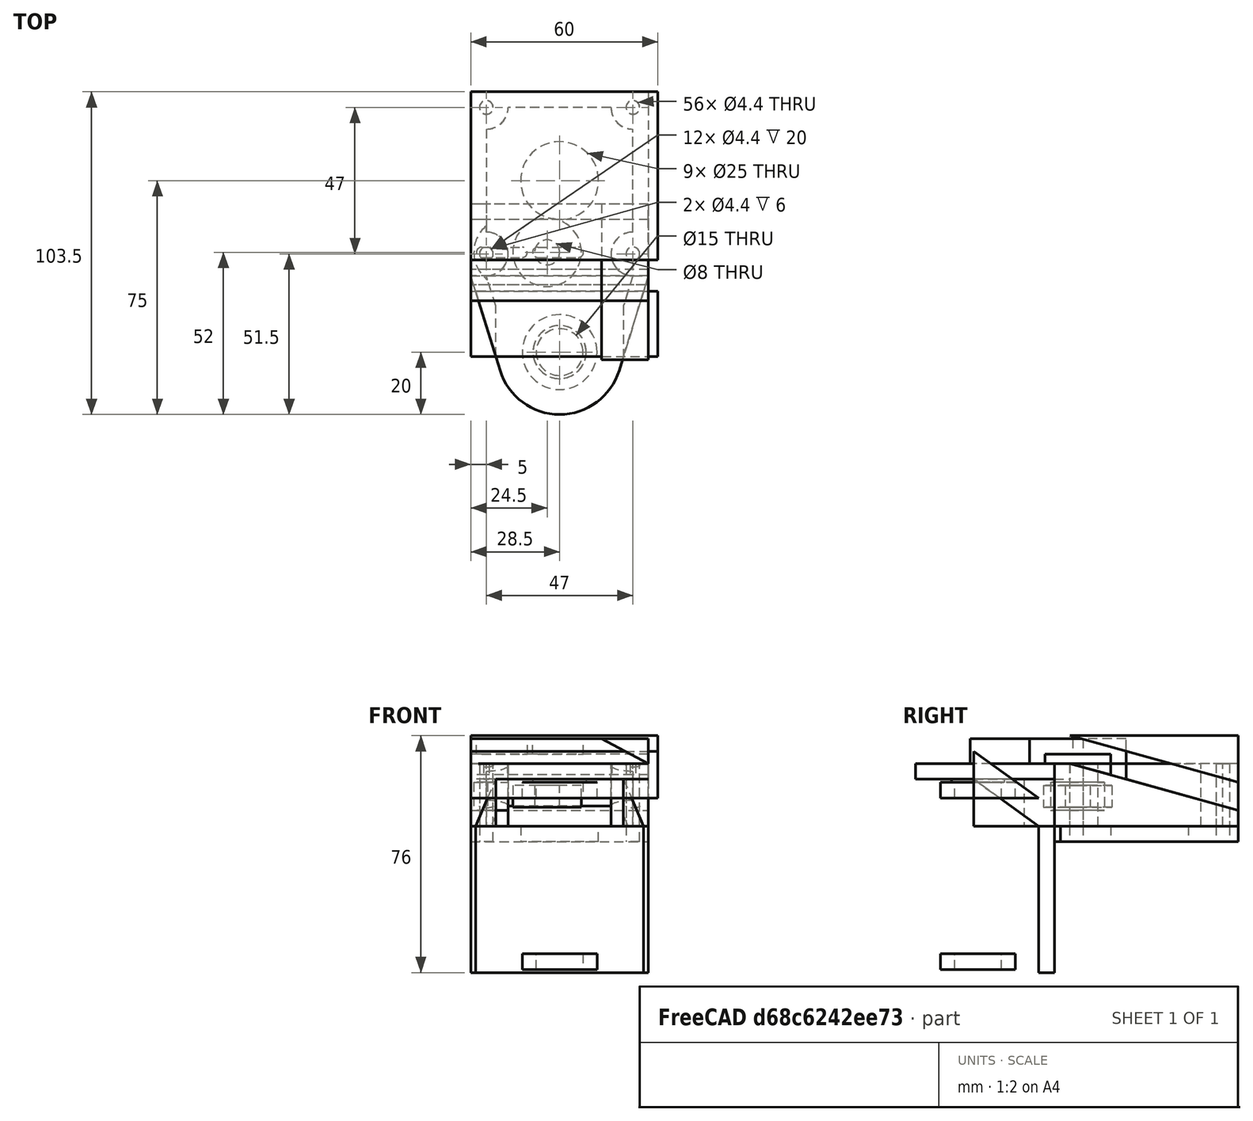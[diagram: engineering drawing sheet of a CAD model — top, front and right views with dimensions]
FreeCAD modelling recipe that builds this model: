
FCSTD DOCUMENT  (FreeCAD 0.16R6700 (Git))
Label: string_drive2_full
License: All rights reserved
LicenseURL: http://en.wikipedia.org/wiki/All_rights_reserved
objects: Sketcher::SketchObject×17, PartDesign::Pad×12, PartDesign::Pocket×5, Mesh::Feature×3, Part::Cylinder×1, Part::FeaturePython×1, Part::Cut×1
note: 54 computed .brp shape members not serialized (recipe doc carries the construction recipe); baked Part::Feature solids carry a one-line shape summary decoded from their .brp

FEATURE [Mesh::Feature] string_guide_full
FEATURE [Part::Cylinder] Cylinder
  Angle = 360
  Height = 5
  Placement = pos=(0,0,5) rot=(0,0,1;0rad)
  Radius = 12
FEATURE [Sketcher::SketchObject] Sketch
  Placement = pos=(0,0,10) rot=(0,0,1;0rad)
  Support = -> Cylinder [Face2]
  sketch-geometry (1):
    g0: Circle CenterX=0 CenterY=0 CenterZ=0 NormalX=0 NormalY=0 NormalZ=1 Radius=7.5
  constraints (2):
    c: Coincident(g0,g-1)
    c: Radius(g0) = 7.5
FEATURE [PartDesign::Pocket] Pocket  label="bearing 6802"
  Length = 5
  Placement = pos=(0,0,5) rot=(0,0,1;0rad)
  Sketch = -> Sketch
  Type = 0
FEATURE [Part::FeaturePython] Clone  label="Clone of bearing 6802"  # Draft clone (typed FeaturePython)
  Objects = -> [Pocket]
  Placement = pos=(0,0,-50) rot=(0,0,1;0rad)
  Scale = (1,1,1)
FEATURE [Mesh::Feature] nema23_76  label="nema23-76"
  Placement = pos=(0,55,-8) rot=(1,0,0;3.14159rad)
FEATURE [Sketcher::SketchObject] Sketch001
  Placement = pos=(0,0,-9) rot=(0,0,1;0rad)
  sketch-geometry (13):
    g0: Circle CenterX=23.5 CenterY=31.5 CenterZ=0 NormalX=0 NormalY=0 NormalZ=1 Radius=2.2
    g1: Circle CenterX=23.5 CenterY=78.5 CenterZ=0 NormalX=0 NormalY=0 NormalZ=1 Radius=2.2
    g2: Circle CenterX=-23.5 CenterY=78.5 CenterZ=0 NormalX=0 NormalY=0 NormalZ=1 Radius=2.2
    g3: Circle CenterX=-23.5 CenterY=31.5 CenterZ=0 NormalX=0 NormalY=0 NormalZ=1 Radius=2.2
    g4: LineSegment [constr] StartX=-23.5 StartY=78.5 StartZ=0 EndX=23.5 EndY=78.5 EndZ=0
    g5: LineSegment [constr] StartX=-23.5 StartY=78.5 StartZ=0 EndX=-23.5 EndY=31.5 EndZ=0
    g6: LineSegment [constr] StartX=-23.5 StartY=31.5 StartZ=0 EndX=23.5 EndY=31.5 EndZ=0
    g7: LineSegment [constr] StartX=23.5 StartY=78.5 StartZ=0 EndX=23.5 EndY=31.5 EndZ=0
    g8: Circle CenterX=0 CenterY=55 CenterZ=0 NormalX=0 NormalY=0 NormalZ=1 Radius=12.5
    g9: LineSegment StartX=-28.5 StartY=83.5 StartZ=0 EndX=28.5 EndY=83.5 EndZ=0
    g10: LineSegment StartX=28.5 StartY=83.5 StartZ=0 EndX=28.5 EndY=26.5 EndZ=0
    g11: LineSegment StartX=28.5 StartY=26.5 StartZ=0 EndX=-28.5 EndY=26.5 EndZ=0
    g12: LineSegment StartX=-28.5 StartY=26.5 StartZ=0 EndX=-28.5 EndY=83.5 EndZ=0
  constraints (35):
    c: Radius(g1) = 2.2
    c: Equal(g1,g2)
    c: Equal(g2,g3)
    c: Equal(g0,g3)
    c: Coincident(g1,g4)
    c: Coincident(g2,g4)
    c: Horizontal(g4)
    c: Coincident(g3,g5)
    c: Coincident(g2,g5)
    c: Vertical(g5)
    c: Coincident(g0,g6)
    c: Coincident(g3,g6)
    c: Horizontal(g6)
    c: Coincident(g0,g7)
    c: Coincident(g1,g7)
    c: Vertical(g7)
    c: DistanceY(g-1,g0) = 31.5
    c: DistanceX(g-1,g0) = 23.5
    c: DistanceX(g3,g0) = 47
    c: DistanceY(g3,g2) = 47
    c: PointOnObject(g8,g-2)
    c: DistanceY(g3,g8) = 23.5
    c: Radius(g8) = 12.5
    c: Coincident(g9,g10)
    c: Coincident(g10,g11)
    c: Coincident(g11,g12)
    c: Coincident(g12,g9)
    c: Horizontal(g9)
    c: Horizontal(g11)
    c: Vertical(g10)
    c: Vertical(g12)
    c: DistanceX(g0,g10) = 5
    c: DistanceY(g10,g0) = 5
    c: DistanceX(g9,g2) = 5
    c: DistanceY(g2,g9) = 5
FEATURE [PartDesign::Pad] Pad
  Length = 5
  Length2 = 100
  Placement = pos=(0,0,-9) rot=(0,0,1;0rad)
  Sketch = -> Sketch001
  Type = 0
FEATURE [Sketcher::SketchObject] Sketch002
  ExternalGeometry = -> [Pad]
  Placement = pos=(0,0,-4) rot=(0,0,1;0rad)
  Support = -> Pad [Face11]
  sketch-geometry (18):
    g0: LineSegment StartX=-28.5 StartY=24.5 StartZ=0 EndX=-28.5 EndY=83.5 EndZ=0
    g1: LineSegment StartX=-28.5 StartY=83.5 StartZ=0 EndX=28.5 EndY=83.5 EndZ=0
    g2: LineSegment StartX=28.5 StartY=83.5 StartZ=0 EndX=28.5 EndY=24.5 EndZ=0
    g3: LineSegment StartX=28.5 StartY=24.5 StartZ=0 EndX=23.5 EndY=24.5 EndZ=0
    g4: LineSegment StartX=23.5 StartY=38.5 StartZ=0 EndX=23.5 EndY=71.5 EndZ=0
    g5: LineSegment StartX=16.5 StartY=78.5 StartZ=0 EndX=-16.5 EndY=78.5 EndZ=0
    g6: LineSegment StartX=-23.5 StartY=71.5 StartZ=0 EndX=-23.5 EndY=38.5 EndZ=0
    g7: LineSegment StartX=-23.5 StartY=24.5 StartZ=0 EndX=-28.5 EndY=24.5 EndZ=0
    g8: ArcOfCircle CenterX=23.5 CenterY=78.5 CenterZ=0 NormalX=0 NormalY=0 NormalZ=1 Radius=7 StartAngle=3.14159 EndAngle=4.71239
    g9: ArcOfCircle CenterX=-23.5 CenterY=78.5 CenterZ=0 NormalX=0 NormalY=0 NormalZ=1 Radius=7 StartAngle=4.71239 EndAngle=6.28319
    g10: ArcOfCircle CenterX=-23.5 CenterY=31.5 CenterZ=0 NormalX=0 NormalY=0 NormalZ=1 Radius=7 StartAngle=4.71239 EndAngle=7.85398
    g11: ArcOfCircle CenterX=23.5 CenterY=31.5 CenterZ=0 NormalX=0 NormalY=0 NormalZ=1 Radius=7 StartAngle=1.5708 EndAngle=4.71239
    g12: LineSegment [constr] StartX=23.5 StartY=38.5 StartZ=0 EndX=23.5 EndY=24.5 EndZ=0
    g13: LineSegment [constr] StartX=-23.5 StartY=38.5 StartZ=0 EndX=-23.5 EndY=24.5 EndZ=0
    g14: Circle CenterX=-23.5 CenterY=78.5 CenterZ=0 NormalX=0 NormalY=0 NormalZ=1 Radius=2.2
    g15: Circle CenterX=23.5 CenterY=78.5 CenterZ=0 NormalX=0 NormalY=0 NormalZ=1 Radius=2.2
    g16: Circle CenterX=23.5 CenterY=31.5 CenterZ=0 NormalX=0 NormalY=0 NormalZ=1 Radius=2.2
    g17: Circle CenterX=-23.5 CenterY=31.5 CenterZ=0 NormalX=0 NormalY=0 NormalZ=1 Radius=2.2
  constraints (46):
    c: Coincident(g0,g1)
    c: Coincident(g1,g2)
    c: Coincident(g-4,g0)
    c: Coincident(g-5,g1)
    c: Horizontal(g7)
    c: Horizontal(g3)
    c: Vertical(g4)
    c: Vertical(g6)
    c: Horizontal(g5)
    c: Radius(g8) = 7
    c: Coincident(g8,g-7)
    c: DistanceX(g3,g3) = 5
    c: DistanceX(g7,g7) = 5
    c: Coincident(g5,g8)
    c: Coincident(g4,g8)
    c: Coincident(g6,g9)
    c: Coincident(g5,g9)
    c: DistanceY(g5,g0) = 5
    c: Radius(g9) = 7
    c: Coincident(g9,g-6)
    c: Coincident(g10,g-8)
    c: Radius(g10) = 7
    c: Equal(g10,g11) = 7
    c: Coincident(g11,g-9)
    c: Coincident(g4,g11)
    c: Coincident(g6,g10)
    c: Coincident(g3,g12)
    c: Coincident(g4,g12)
    c: Vertical(g12)
    c: Coincident(g7,g13)
    c: Coincident(g6,g13)
    c: Vertical(g13)
    c: Coincident(g14,g9)
    c: Radius(g14) = 2.2
    c: Coincident(g8,g15)
    c: Radius(g15) = 2.2
    c: Coincident(g11,g16)
    c: Radius(g16) = 2.2
    c: Coincident(g10,g17)
    c: Radius(g17) = 2.2
    c: Coincident(g0,g7)
    c: Coincident(g7,g10)
    c: Vertical(g0)
    c: Coincident(g2,g3)
    c: Coincident(g11,g3)
    c: Vertical(g2)
FEATURE [PartDesign::Pad] Pad001
  Length = 20
  Length2 = 100
  Placement = pos=(0,0,-9) rot=(0,0,1;0rad)
  Sketch = -> Sketch002
  Type = 0
FEATURE [Sketcher::SketchObject] Sketch005
  ExternalGeometry = -> [Pad001]
  Placement = pos=(-28.5,0,-9) rot=(0.57735,-0.57735,-0.57735;2.0944rad)
  Support = -> Pad001 [Face16]
  sketch-geometry (5):
    g0: LineSegment StartX=-83.5 StartY=25 StartZ=0 EndX=-29.5 EndY=25 EndZ=0
    g1: LineSegment StartX=-29.5 StartY=25 StartZ=0 EndX=-83.5 EndY=10 EndZ=0
    g2: LineSegment StartX=-83.5 StartY=10 StartZ=0 EndX=-83.5 EndY=25 EndZ=0
    g3: LineSegment [constr] StartX=-83.5 StartY=5 StartZ=0 EndX=-83.5 EndY=10 EndZ=0
    g4: LineSegment [constr] StartX=-29.5 StartY=25 StartZ=0 EndX=-24.5 EndY=25 EndZ=0
  constraints (12):
    c: Coincident(g0,g2)
    c: Coincident(g0,g-4)
    c: Coincident(g1,g2)
    c: Coincident(g1,g3)
    c: Vertical(g3)
    c: Coincident(g3,g-4)
    c: DistanceY(g3,g3) = 5
    c: Coincident(g0,g1)
    c: Coincident(g4,g-3)
    c: Coincident(g4,g0)
    c: Distance(g4) = 5
    c: Horizontal(g4)
FEATURE [PartDesign::Pocket] Pocket001
  Length = 60
  Placement = pos=(0,0,-9) rot=(0,0,1;0rad)
  Sketch = -> Sketch005
  Type = 0
FEATURE [Sketcher::SketchObject] Sketch006
  ExternalGeometry = -> [Pocket001]
  Placement = pos=(0,0,16) rot=(0,0,1;0rad)
  Support = -> Pocket001 [Face32]
  sketch-geometry (6):
    g0: LineSegment StartX=-28.5 StartY=29.5 StartZ=0 EndX=28.5 EndY=29.5 EndZ=0
    g1: LineSegment StartX=28.5 StartY=29.5 StartZ=0 EndX=28.5 EndY=24.5 EndZ=0
    g2: LineSegment StartX=28.5 StartY=24.5 StartZ=0 EndX=19.1092 EndY=-5.90251 EndZ=0
    g3: LineSegment StartX=-19.1092 StartY=-5.90251 StartZ=0 EndX=-28.5 EndY=24.5 EndZ=0
    g4: LineSegment StartX=-28.5 StartY=24.5 StartZ=0 EndX=-28.5 EndY=29.5 EndZ=0
    g5: ArcOfCircle CenterX=0 CenterY=0 CenterZ=0 NormalX=0 NormalY=0 NormalZ=1 Radius=20 StartAngle=3.44118 EndAngle=5.9836
  constraints (12):
    c: Coincident(g1,g2)
    c: Coincident(g3,g4)
    c: Coincident(g0,g4)
    c: Coincident(g0,g1)
    c: Coincident(g0,g-4)
    c: Coincident(g1,g-4)
    c: Coincident(g0,g-3)
    c: Coincident(g3,g-3)
    c: Tangent(g3,g5) = 1.5708
    c: Tangent(g2,g5) = 1.5708
    c: Coincident(g5,g-1)
    c: Radius(g5) = 20
FEATURE [PartDesign::Pad] Pad002
  Length = 5
  Length2 = 100
  Placement = pos=(0,0,-9) rot=(0,0,1;0rad)
  Reversed = true
  Sketch = -> Sketch006
  Type = 0
FEATURE [Sketcher::SketchObject] Sketch007
  ExternalGeometry = -> [Pad002]
  Placement = pos=(0,0,11) rot=(1,0,0;3.14159rad)
  Support = -> Pad002 [Face39]
  sketch-geometry (8):
    g0: LineSegment StartX=-28.5 StartY=-24.5 StartZ=0 EndX=-20.5 EndY=1.39974 EndZ=0
    g1: LineSegment StartX=-20.5 StartY=1.39974 StartZ=0 EndX=-20.5 EndY=-14.7876 EndZ=0
    g2: LineSegment StartX=-20.5 StartY=-14.7876 StartZ=0 EndX=-23.5 EndY=-24.5 EndZ=0
    g3: LineSegment StartX=-23.5 StartY=-24.5 StartZ=0 EndX=-28.5 EndY=-24.5 EndZ=0
    g4: LineSegment StartX=28.5 StartY=-24.5 StartZ=0 EndX=23.5 EndY=-24.5 EndZ=0
    g5: LineSegment StartX=23.5 StartY=-24.5 StartZ=0 EndX=20.5 EndY=-14.7876 EndZ=0
    g6: LineSegment StartX=20.5 StartY=-14.7876 StartZ=0 EndX=20.5 EndY=1.39974 EndZ=0
    g7: LineSegment StartX=20.5 StartY=1.39974 StartZ=0 EndX=28.5 EndY=-24.5 EndZ=0
  constraints (22):
    c: Coincident(g0,g1)
    c: Coincident(g1,g2)
    c: Coincident(g2,g3)
    c: Coincident(g3,g0)
    c: Horizontal(g3)
    c: DistanceX(g3,g3) = 5
    c: Coincident(g0,g-5)
    c: PointOnObject(g0,g-5)
    c: Parallel(g-5,g2)
    c: Vertical(g1)
    c: DistanceX(g2,g1) = 3
    c: Coincident(g4,g5)
    c: Coincident(g5,g6)
    c: Coincident(g6,g7)
    c: Coincident(g7,g4)
    c: Horizontal(g4)
    c: DistanceX(g4,g4) = 5
    c: DistanceX(g5,g4) = 3
    c: Vertical(g6)
    c: Coincident(g4,g-6)
    c: PointOnObject(g6,g-6)
    c: Parallel(g-6,g5)
FEATURE [PartDesign::Pad] Pad003
  Length = 15
  Length2 = 100
  Placement = pos=(0,0,-9) rot=(0,0,1;0rad)
  Sketch = -> Sketch007
  Type = 0
FEATURE [Sketcher::SketchObject] Sketch008
  ExternalGeometry = -> [Pad003]
  Placement = pos=(-28.5,0,-9) rot=(0.57735,-0.57735,-0.57735;2.0944rad)
  Support = -> Pad003 [Face16]
  sketch-geometry (4):
    g0: LineSegment StartX=-19.5 StartY=5 StartZ=0 EndX=1.39974 EndY=20 EndZ=0
    g1: LineSegment StartX=1.39974 StartY=20 StartZ=0 EndX=1.39974 EndY=5 EndZ=0
    g2: LineSegment StartX=1.39974 StartY=5 StartZ=0 EndX=-19.5 EndY=5 EndZ=0
    g3: LineSegment [constr] StartX=-24.5 StartY=5 StartZ=0 EndX=-19.5 EndY=5 EndZ=0
  constraints (9):
    c: Coincident(g0,g1)
    c: Coincident(g1,g2)
    c: Coincident(g0,g-4)
    c: Coincident(g1,g-4)
    c: Coincident(g0,g2)
    c: Coincident(g0,g3)
    c: Horizontal(g3)
    c: DistanceX(g3,g3) = 5
    c: Coincident(g3,g-3)
FEATURE [PartDesign::Pocket] Pocket002
  Length = 60
  Placement = pos=(0,0,-9) rot=(0,0,1;0rad)
  Sketch = -> Sketch008
  Type = 0
FEATURE [Sketcher::SketchObject] Sketch009
  Placement = pos=(0,0,11) rot=(1,0,0;3.14159rad)
  Support = -> Pocket002 [Face45]
  sketch-geometry (1):
    g0: Circle CenterX=0 CenterY=0 CenterZ=0 NormalX=0 NormalY=0 NormalZ=1 Radius=8.5
  constraints (2):
    c: Coincident(g0,g-1)
    c: Radius(g0) = 8.5
FEATURE [PartDesign::Pad] Pad004
  Length = 1
  Length2 = 100
  Placement = pos=(0,0,-9) rot=(0,0,1;0rad)
  Sketch = -> Sketch009
  Type = 0
FEATURE [Sketcher::SketchObject] Sketch010
  Placement = pos=(-20.5,0,-9) rot=(0.57735,0.57735,0.57735;2.0944rad)
  Support = -> Pad004 [Face55]
  sketch-geometry (1):
    g0: Circle CenterX=0 CenterY=0 CenterZ=0 NormalX=0 NormalY=0 NormalZ=1 Radius=7.5
  constraints (2):
    c: Coincident(g0,g-1)
    c: Radius(g0) = 7.5
FEATURE [PartDesign::Pad] Pad005
  Length = 5
  Length2 = 100
  Placement = pos=(0,0,-9) rot=(0,0,1;0rad)
  Sketch = -> Sketch010
  Type = 0
FEATURE [Sketcher::SketchObject] Sketch011
  ExternalGeometry = -> [Pad005]
  Placement = pos=(0,0,-4) rot=(1,0,0;3.14159rad)
  Support = -> Pad005 [Face13]
  sketch-geometry (4):
    g0: LineSegment StartX=-28.5 StartY=-24.5 StartZ=0 EndX=28.5 EndY=-24.5 EndZ=0
    g1: LineSegment StartX=28.5 StartY=-24.5 StartZ=0 EndX=26.9556 EndY=-19.5 EndZ=0
    g2: LineSegment StartX=26.9556 StartY=-19.5 StartZ=0 EndX=-26.9556 EndY=-19.5 EndZ=0
    g3: LineSegment StartX=-26.9556 StartY=-19.5 StartZ=0 EndX=-28.5 EndY=-24.5 EndZ=0
  constraints (10):
    c: Coincident(g0,g1)
    c: Coincident(g1,g2)
    c: Coincident(g2,g3)
    c: Coincident(g3,g0)
    c: Horizontal(g0)
    c: Horizontal(g2)
    c: Coincident(g-5,g0)
    c: Coincident(g2,g-5)
    c: Coincident(g1,g-6)
    c: Coincident(g0,g-6)
FEATURE [PartDesign::Pad] Pad006
  Length = 47
  Length2 = 100
  Placement = pos=(0,0,-9) rot=(0,0,1;0rad)
  Sketch = -> Sketch011
  Type = 0
FEATURE [Sketcher::SketchObject] Sketch012
  ExternalGeometry = -> [Pad006]
  Placement = pos=(0,26.5,-9) rot=(1,0,0;1.5708rad)
  Support = -> Pad006 [Face4]
  sketch-geometry (4):
    g0: LineSegment StartX=-28.5 StartY=5 StartZ=0 EndX=28.5 EndY=5 EndZ=0
    g1: LineSegment StartX=28.5 StartY=5 StartZ=0 EndX=28.5 EndY=0 EndZ=0
    g2: LineSegment StartX=28.5 StartY=0 StartZ=0 EndX=-28.5 EndY=0 EndZ=0
    g3: LineSegment StartX=-28.5 StartY=0 StartZ=0 EndX=-28.5 EndY=5 EndZ=0
  constraints (10):
    c: Coincident(g0,g1)
    c: Coincident(g1,g2)
    c: Coincident(g2,g3)
    c: Coincident(g3,g0)
    c: Horizontal(g0)
    c: Horizontal(g2)
    c: Vertical(g1)
    c: Vertical(g3)
    c: Coincident(g0,g-4)
    c: Coincident(g2,g-3)
FEATURE [PartDesign::Pad] Pad007
  Length = 2
  Length2 = 100
  Placement = pos=(0,0,-9) rot=(0,0,1;0rad)
  Sketch = -> Sketch012
  Type = 0
FEATURE [Sketcher::SketchObject] Sketch013
  Placement = pos=(0,0,10) rot=(1,0,0;3.14159rad)
  Support = -> Pad007 [Face62]
  sketch-geometry (1):
    g0: Circle CenterX=0 CenterY=0 CenterZ=0 NormalX=0 NormalY=0 NormalZ=1 Radius=7.5
  constraints (2):
    c: Coincident(g-1,g0)
    c: Radius(g0) = 7.5
FEATURE [PartDesign::Pad] Pad008
  Length = 5
  Length2 = 100
  Placement = pos=(0,0,-9) rot=(0,0,1;0rad)
  Sketch = -> Sketch013
  Type = 0
FEATURE [Sketcher::SketchObject] Sketch014
  Placement = pos=(-4,32,2) rot=(0,0,1;0rad)
  sketch-geometry (2):
    g0: Circle CenterX=0 CenterY=0 CenterZ=0 NormalX=0 NormalY=0 NormalZ=1 Radius=4
    g1: Circle CenterX=0 CenterY=0 CenterZ=0 NormalX=0 NormalY=0 NormalZ=1 Radius=11
  constraints (4):
    c: Coincident(g-1,g0)
    c: Radius(g0) = 4
    c: Radius(g1) = 11
    c: Coincident(g1,g-1)
FEATURE [PartDesign::Pad] Pad009  label="608 bearing"
  Length = 7
  Length2 = 100
  Placement = pos=(-4,32,2) rot=(0,0,1;0rad)
  Sketch = -> Sketch014
  Type = 0
FEATURE [Sketcher::SketchObject] Sketch015
  ExternalGeometry = -> [Pad008]
  Placement = pos=(-4,32,9) rot=(0,0,1;0rad)
  Support = -> Pad009 [Face4]
  sketch-geometry (3):
    g0: Circle CenterX=-12.5 CenterY=0 CenterZ=0 NormalX=0 NormalY=0 NormalZ=1 Radius=11
    g1: LineSegment [constr] StartX=-12.5 StartY=0 StartZ=0 EndX=-24.5 EndY=0 EndZ=0
    g2: GeomPoint [constr] X=-23.5 Y=0 Z=0
  constraints (8):
    c: Radius(g0) = 11
    c: Coincident(g0,g1)
    c: Horizontal(g1)
    c: PointOnObject(g0,g-1)
    c: PointOnObject(g2,g0)
    c: PointOnObject(g2,g1)
    c: Distance(g2,g1) = 1
    c: PointOnObject(g1,g-3)
FEATURE [PartDesign::Pad] Pad010
  Length = 1
  Length2 = 8
  Placement = pos=(-4,32,2) rot=(0,0,1;0rad)
  Reversed = true
  Sketch = -> Sketch015
  Type = 4
FEATURE [Part::Cut] Cut
  Base = -> Pad008
  Tool = -> Pad010
FEATURE [Mesh::Feature] bearing_holder
  Placement = pos=(-4,32,19) rot=(1,0,0;3.14159rad)
FEATURE [Sketcher::SketchObject] Sketch016
  ExternalGeometry = -> [Cut]
  Placement = pos=(28.5,0,0) rot=(0.57735,0.57735,0.57735;2.0944rad)
  Support = -> Cut [Face14]
  sketch-geometry (8):
    g0: LineSegment StartX=21.5 StartY=19 StartZ=0 EndX=21.5 EndY=16 EndZ=0
    g1: LineSegment StartX=21.5 StartY=19 StartZ=0 EndX=42.5 EndY=19 EndZ=0
    g2: LineSegment StartX=42.5 StartY=19 StartZ=0 EndX=42.5 EndY=12.3889 EndZ=0
    g3: LineSegment StartX=42.5 StartY=12.3889 StartZ=0 EndX=47.5 EndY=11 EndZ=0
    g4: LineSegment StartX=47.5 StartY=11 StartZ=0 EndX=47.5 EndY=24 EndZ=0
    g5: LineSegment StartX=47.5 StartY=24 StartZ=0 EndX=16.5 EndY=24 EndZ=0
    g6: LineSegment StartX=16.5 StartY=24 StartZ=0 EndX=16.5 EndY=16 EndZ=0
    g7: LineSegment StartX=16.5 StartY=16 StartZ=0 EndX=21.5 EndY=16 EndZ=0
  constraints (24):
    c: Coincident(g2,g3)
    c: Coincident(g3,g4)
    c: Coincident(g4,g5)
    c: Coincident(g5,g6)
    c: Coincident(g6,g7)
    c: Coincident(g0,g7)
    c: Coincident(g1,g2)
    c: Coincident(g0,g1)
    c: PointOnObject(g2,g-4)
    c: PointOnObject(g3,g-4)
    c: Vertical(g2)
    c: Vertical(g4)
    c: Vertical(g6)
    c: Vertical(g0)
    c: PointOnObject(g6,g-3)
    c: PointOnObject(g0,g-3)
    c: Horizontal(g1)
    c: DistanceY(g1,g4) = 5
    c: DistanceX(g7,g7) = 5
    c: DistanceX(g2,g3) = 5
    c: DistanceX(g0,g-3) = 3
    c: DistanceX(g-4,g2) = 13
    c: Horizontal(g5)
    c: DistanceY(g0,g0) = 3
FEATURE [PartDesign::Pad] Pad011
  Length = 57
  Length2 = 100
  Reversed = true
  Sketch = -> Sketch016
  Type = 0
FEATURE [Sketcher::SketchObject] Sketch017
  ExternalGeometry = -> [Pad011]
  Placement = pos=(0,47.5,0) rot=(0,0.707107,0.707107;3.14159rad)
  Support = -> Pad011 [Face15]
  sketch-geometry (3):
    g0: LineSegment StartX=-28.5 StartY=24 StartZ=0 EndX=-28.5 EndY=16 EndZ=0
    g1: LineSegment StartX=-28.5 StartY=16 StartZ=0 EndX=-13.5 EndY=24 EndZ=0
    g2: LineSegment StartX=-13.5 StartY=24 StartZ=0 EndX=-28.5 EndY=24 EndZ=0
  constraints (8):
    c: Coincident(g0,g1)
    c: Coincident(g1,g2)
    c: Coincident(g0,g2)
    c: Coincident(g0,g-3)
    c: PointOnObject(g0,g-3)
    c: DistanceX(g2,g2) = 15
    c: DistanceY(g-3,g0) = 5
    c: Horizontal(g2)
FEATURE [PartDesign::Pocket] Pocket003
  Length = 50
  Sketch = -> Sketch017
  Type = 0
FEATURE [Sketcher::SketchObject] Sketch020
  Placement = pos=(0,0,24) rot=(0,0,1;0rad)
  Support = -> Pocket003 [Face8]
  sketch-geometry (8):
    g0: ArcOfCircle CenterX=-25 CenterY=32 CenterZ=0 NormalX=0 NormalY=0 NormalZ=1 Radius=1.65 StartAngle=1.5708 EndAngle=4.71239
    g1: ArcOfCircle CenterX=-12 CenterY=32 CenterZ=0 NormalX=0 NormalY=0 NormalZ=1 Radius=1.65 StartAngle=4.71239 EndAngle=7.85398
    g2: LineSegment StartX=-25 StartY=30.35 StartZ=0 EndX=-12 EndY=30.35 EndZ=0
    g3: LineSegment StartX=-25 StartY=33.65 StartZ=0 EndX=-12 EndY=33.65 EndZ=0
    g4: ArcOfCircle CenterX=-7 CenterY=32 CenterZ=0 NormalX=0 NormalY=0 NormalZ=1 Radius=1.65 StartAngle=1.5708 EndAngle=4.71239
    g5: ArcOfCircle CenterX=6 CenterY=32 CenterZ=0 NormalX=0 NormalY=0 NormalZ=1 Radius=1.65 StartAngle=4.71239 EndAngle=7.85398
    g6: LineSegment StartX=-7 StartY=30.35 StartZ=0 EndX=6 EndY=30.35 EndZ=0
    g7: LineSegment StartX=-7 StartY=33.65 StartZ=0 EndX=6 EndY=33.65 EndZ=0
  constraints (20):
    c: Tangent(g0,g3) = 1.5708
    c: Tangent(g0,g2) = -1.5708
    c: Tangent(g2,g1) = -1.5708
    c: Tangent(g3,g1) = 1.5708
    c: Horizontal(g2)
    c: Equal(g0,g1)
    c: Tangent(g4,g7) = 1.5708
    c: Tangent(g4,g6) = -1.5708
    c: Tangent(g6,g5) = -1.5708
    c: Tangent(g7,g5) = 1.5708
    c: Horizontal(g6)
    c: Equal(g4,g5)
    c: DistanceY(g-1,g4) = 32
    c: DistanceY(g-1,g0) = 32
    c: DistanceY(g0,g0) = 3.3
    c: DistanceY(g4,g4) = 3.3
    c: DistanceX(g0,g1) = 13
    c: DistanceX(g4,g5) = 13
    c: DistanceX(g0,g-1) = 25
    c: DistanceX(g1,g4) = 5
FEATURE [PartDesign::Pocket] Pocket006
  Length = 5
  Sketch = -> Sketch020
  Type = 0
